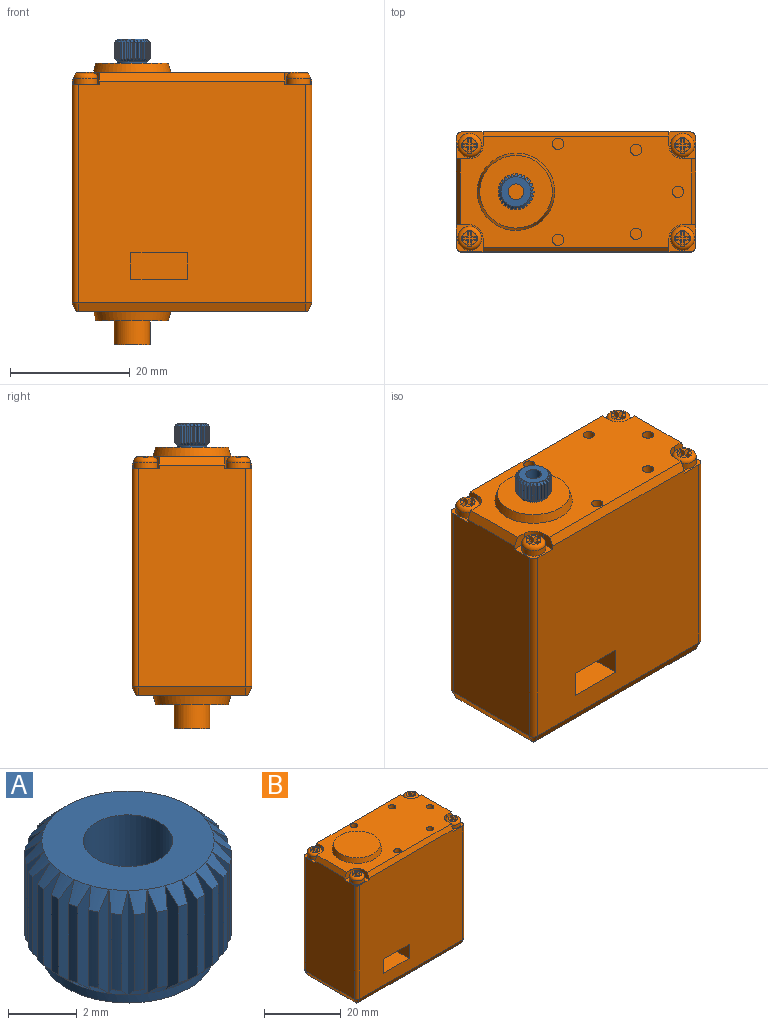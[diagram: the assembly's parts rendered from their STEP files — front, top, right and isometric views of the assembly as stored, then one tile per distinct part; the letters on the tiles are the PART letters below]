
ASSEMBLY  parts=2 mates=1
PART A: 144 faces, bbox 6x6x4 mm
  f0: cone r=3mm half-angle=45deg, axis (0,0,-1), area 0.3mm2, adj f1,f5,f7,f8
  f1: cylinder r=3mm len=2.7mm, axis (0,0,1), area 0.8mm2, adj f0,f2,f7,f8
  f2: cone r=2.5mm half-angle=45deg, axis (0,0,1), area 0.3mm2, adj f1,f6,f7,f8
  f3: plane 5x5mm, normal (0,0,-1), area 14.3mm2, adj f4,f6
  f4: cylinder r=1.3mm len=4mm, axis (0,0,1), area 32.7mm2, adj f3,f5
  f5: plane 5x5mm, normal (0,0,1), area 14.3mm2, adj f0,f4,f9,f14,f19,f24,f29,f34
  f6: cylinder r=2.5mm len=5mm, axis (0,0,1), area 4.7mm2, adj f2,f3,f11,f16,f21,f26,f31,f36
  f7: plane 3.72x0.53mm, normal (-0.23,0.97,0), area 1.7mm2, adj f0,f1,f2,f13
  f8: plane 3.72x0.53mm, normal (-0.23,-0.97,0), area 1.7mm2, adj f0,f1,f2,f142
  f9: cone r=3mm half-angle=45deg, axis (0,0,-1), area 0.3mm2, adj f5,f10,f12,f13
  f10: cylinder r=3mm len=2.7mm, axis (0,0,1), area 0.8mm2, adj f9,f11,f12,f13
  f11: cone r=2.5mm half-angle=45deg, axis (0,0,1), area 0.3mm2, adj f6,f10,f12,f13
  f12: plane 3.72x0.54mm, normal (-0.01,1,0), area 1.7mm2, adj f9,f10,f11,f18
  f13: plane 3.72x0.49mm, normal (-0.45,-0.9,0), area 1.7mm2, adj f7,f9,f10,f11
  f14: cone r=3mm half-angle=45deg, axis (0,0,-1), area 0.3mm2, adj f5,f15,f17,f18
  f15: cylinder r=3mm len=2.7mm, axis (0,0,1), area 0.8mm2, adj f14,f16,f17,f18
  f16: cone r=2.5mm half-angle=45deg, axis (0,0,1), area 0.3mm2, adj f6,f15,f17,f18
  f17: plane 3.72x0.53mm, normal (0.21,0.98,0), area 1.7mm2, adj f14,f15,f16,f23
  f18: plane 3.72x0.42mm, normal (-0.63,-0.77,0), area 1.7mm2, adj f12,f14,f15,f16
  f19: cone r=3mm half-angle=45deg, axis (0,0,-1), area 0.3mm2, adj f5,f20,f22,f23
  f20: cylinder r=3mm len=2.7mm, axis (0,0,1), area 0.8mm2, adj f19,f21,f22,f23
  f21: cone r=2.5mm half-angle=45deg, axis (0,0,1), area 0.3mm2, adj f6,f20,f22,f23
  f22: plane 3.72x0.49mm, normal (0.42,0.91,0), area 1.7mm2, adj f19,f20,f21,f28
  f23: plane 3.72x0.43mm, normal (-0.79,-0.61,0), area 1.7mm2, adj f17,f19,f20,f21
  f24: cone r=3mm half-angle=45deg, axis (0,0,-1), area 0.3mm2, adj f5,f25,f27,f28
  f25: cylinder r=3mm len=2.7mm, axis (0,0,1), area 0.8mm2, adj f24,f26,f27,f28
  f26: cone r=2.5mm half-angle=45deg, axis (0,0,1), area 0.3mm2, adj f6,f25,f27,f28
  f27: plane 3.72x0.43mm, normal (0.61,0.79,0), area 1.7mm2, adj f24,f25,f26,f33
  f28: plane 3.72x0.49mm, normal (-0.91,-0.42,0), area 1.7mm2, adj f22,f24,f25,f26
  f29: cone r=3mm half-angle=45deg, axis (0,0,-1), area 0.3mm2, adj f5,f30,f32,f33
  f30: cylinder r=3mm len=2.7mm, axis (0,0,1), area 0.8mm2, adj f29,f31,f32,f33
  f31: cone r=2.5mm half-angle=45deg, axis (0,0,1), area 0.3mm2, adj f6,f30,f32,f33
  f32: plane 3.72x0.42mm, normal (0.77,0.63,0), area 1.7mm2, adj f29,f30,f31,f38
  f33: plane 3.72x0.53mm, normal (-0.98,-0.21,0), area 1.7mm2, adj f27,f29,f30,f31
  f34: cone r=3mm half-angle=45deg, axis (0,0,-1), area 0.3mm2, adj f5,f35,f37,f38
  f35: cylinder r=3mm len=2.7mm, axis (0,0,1), area 0.8mm2, adj f34,f36,f37,f38
  f36: cone r=2.5mm half-angle=45deg, axis (0,0,1), area 0.3mm2, adj f6,f35,f37,f38
  f37: plane 3.72x0.49mm, normal (0.9,0.45,0), area 1.7mm2, adj f34,f35,f36,f43
  f38: plane 3.72x0.54mm, normal (-1,0.01,0), area 1.7mm2, adj f32,f34,f35,f36
  f39: cone r=3mm half-angle=45deg, axis (0,0,-1), area 0.3mm2, adj f5,f40,f42,f43
  f40: cylinder r=3mm len=2.7mm, axis (0,0,1), area 0.8mm2, adj f39,f41,f42,f43
  f41: cone r=2.5mm half-angle=45deg, axis (0,0,1), area 0.3mm2, adj f6,f40,f42,f43
  f42: plane 3.72x0.53mm, normal (0.97,0.23,0), area 1.7mm2, adj f39,f40,f41,f48
  f43: plane 3.72x0.53mm, normal (-0.97,0.23,0), area 1.7mm2, adj f37,f39,f40,f41
  f44: cone r=3mm half-angle=45deg, axis (0,0,-1), area 0.3mm2, adj f5,f45,f47,f48
  f45: cylinder r=3mm len=2.7mm, axis (0,0,1), area 0.8mm2, adj f44,f46,f47,f48
  f46: cone r=2.5mm half-angle=45deg, axis (0,0,1), area 0.3mm2, adj f6,f45,f47,f48
  f47: plane 3.72x0.54mm, normal (1,0.01,0), area 1.7mm2, adj f44,f45,f46,f53
  f48: plane 3.72x0.49mm, normal (-0.9,0.45,0), area 1.7mm2, adj f42,f44,f45,f46
  f49: cone r=3mm half-angle=45deg, axis (0,0,-1), area 0.3mm2, adj f5,f50,f52,f53
  f50: cylinder r=3mm len=2.7mm, axis (0,0,1), area 0.8mm2, adj f49,f51,f52,f53
  f51: cone r=2.5mm half-angle=45deg, axis (0,0,1), area 0.3mm2, adj f6,f50,f52,f53
  f52: plane 3.72x0.53mm, normal (0.98,-0.21,0), area 1.7mm2, adj f49,f50,f51,f58
  f53: plane 3.72x0.42mm, normal (-0.77,0.63,0), area 1.7mm2, adj f47,f49,f50,f51
  f54: cone r=3mm half-angle=45deg, axis (0,0,-1), area 0.3mm2, adj f5,f55,f57,f58
  f55: cylinder r=3mm len=2.7mm, axis (0,0,1), area 0.8mm2, adj f54,f56,f57,f58
  f56: cone r=2.5mm half-angle=45deg, axis (0,0,1), area 0.3mm2, adj f6,f55,f57,f58
  f57: plane 3.72x0.49mm, normal (0.91,-0.42,0), area 1.7mm2, adj f54,f55,f56,f63
  f58: plane 3.72x0.43mm, normal (-0.61,0.79,0), area 1.7mm2, adj f52,f54,f55,f56
  f59: cone r=3mm half-angle=45deg, axis (0,0,-1), area 0.3mm2, adj f5,f60,f62,f63
  f60: cylinder r=3mm len=2.7mm, axis (0,0,1), area 0.8mm2, adj f59,f61,f62,f63
  f61: cone r=2.5mm half-angle=45deg, axis (0,0,1), area 0.3mm2, adj f6,f60,f62,f63
  f62: plane 3.72x0.43mm, normal (0.79,-0.61,0), area 1.7mm2, adj f59,f60,f61,f68
  f63: plane 3.72x0.49mm, normal (-0.42,0.91,0), area 1.7mm2, adj f57,f59,f60,f61
  f64: cone r=3mm half-angle=45deg, axis (0,0,-1), area 0.3mm2, adj f5,f65,f67,f68
  f65: cylinder r=3mm len=2.7mm, axis (0,0,1), area 0.8mm2, adj f64,f66,f67,f68
  f66: cone r=2.5mm half-angle=45deg, axis (0,0,1), area 0.3mm2, adj f6,f65,f67,f68
  f67: plane 3.72x0.42mm, normal (0.63,-0.77,0), area 1.7mm2, adj f64,f65,f66,f73
  f68: plane 3.72x0.53mm, normal (-0.21,0.98,0), area 1.7mm2, adj f62,f64,f65,f66
  f69: cone r=3mm half-angle=45deg, axis (0,0,-1), area 0.3mm2, adj f5,f70,f72,f73
  f70: cylinder r=3mm len=2.7mm, axis (0,0,1), area 0.8mm2, adj f69,f71,f72,f73
  f71: cone r=2.5mm half-angle=45deg, axis (0,0,1), area 0.3mm2, adj f6,f70,f72,f73
  f72: plane 3.72x0.49mm, normal (0.45,-0.9,0), area 1.7mm2, adj f69,f70,f71,f78
  f73: plane 3.72x0.54mm, normal (0.01,1,0), area 1.7mm2, adj f67,f69,f70,f71
  f74: cone r=3mm half-angle=45deg, axis (0,0,-1), area 0.3mm2, adj f5,f75,f77,f78
  f75: cylinder r=3mm len=2.7mm, axis (0,0,1), area 0.8mm2, adj f74,f76,f77,f78
  f76: cone r=2.5mm half-angle=45deg, axis (0,0,1), area 0.3mm2, adj f6,f75,f77,f78
  f77: plane 3.72x0.53mm, normal (0.23,-0.97,0), area 1.7mm2, adj f74,f75,f76,f83
  f78: plane 3.72x0.53mm, normal (0.23,0.97,0), area 1.7mm2, adj f72,f74,f75,f76
  f79: cone r=3mm half-angle=45deg, axis (0,0,-1), area 0.3mm2, adj f5,f80,f82,f83
  f80: cylinder r=3mm len=2.7mm, axis (0,0,1), area 0.8mm2, adj f79,f81,f82,f83
  f81: cone r=2.5mm half-angle=45deg, axis (0,0,1), area 0.3mm2, adj f6,f80,f82,f83
  f82: plane 3.72x0.54mm, normal (0.01,-1,0), area 1.7mm2, adj f79,f80,f81,f88
  f83: plane 3.72x0.49mm, normal (0.45,0.9,0), area 1.7mm2, adj f77,f79,f80,f81
  f84: cone r=3mm half-angle=45deg, axis (0,0,-1), area 0.3mm2, adj f5,f85,f87,f88
  f85: cylinder r=3mm len=2.7mm, axis (0,0,1), area 0.8mm2, adj f84,f86,f87,f88
  f86: cone r=2.5mm half-angle=45deg, axis (0,0,1), area 0.3mm2, adj f6,f85,f87,f88
  f87: plane 3.72x0.53mm, normal (-0.21,-0.98,0), area 1.7mm2, adj f84,f85,f86,f93
  f88: plane 3.72x0.42mm, normal (0.63,0.77,0), area 1.7mm2, adj f82,f84,f85,f86
  f89: cone r=3mm half-angle=45deg, axis (0,0,-1), area 0.3mm2, adj f5,f90,f92,f93
  f90: cylinder r=3mm len=2.7mm, axis (0,0,1), area 0.8mm2, adj f89,f91,f92,f93
  f91: cone r=2.5mm half-angle=45deg, axis (0,0,1), area 0.3mm2, adj f6,f90,f92,f93
  f92: plane 3.72x0.49mm, normal (-0.42,-0.91,0), area 1.7mm2, adj f89,f90,f91,f98
  f93: plane 3.72x0.43mm, normal (0.79,0.61,0), area 1.7mm2, adj f87,f89,f90,f91
  f94: cone r=3mm half-angle=45deg, axis (0,0,-1), area 0.3mm2, adj f5,f95,f97,f98
  f95: cylinder r=3mm len=2.7mm, axis (0,0,1), area 0.8mm2, adj f94,f96,f97,f98
  f96: cone r=2.5mm half-angle=45deg, axis (0,0,1), area 0.3mm2, adj f6,f95,f97,f98
  f97: plane 3.72x0.43mm, normal (-0.61,-0.79,0), area 1.7mm2, adj f94,f95,f96,f103
  f98: plane 3.72x0.49mm, normal (0.91,0.42,0), area 1.7mm2, adj f92,f94,f95,f96
  f99: cone r=3mm half-angle=45deg, axis (0,0,-1), area 0.3mm2, adj f5,f100,f102,f103
  f100: cylinder r=3mm len=2.7mm, axis (0,0,1), area 0.8mm2, adj f99,f101,f102,f103
  f101: cone r=2.5mm half-angle=45deg, axis (0,0,1), area 0.3mm2, adj f6,f100,f102,f103
  f102: plane 3.72x0.42mm, normal (-0.77,-0.63,0), area 1.7mm2, adj f99,f100,f101,f108
  f103: plane 3.72x0.53mm, normal (0.98,0.21,0), area 1.7mm2, adj f97,f99,f100,f101
  f104: cone r=3mm half-angle=45deg, axis (0,0,-1), area 0.3mm2, adj f5,f105,f107,f108
  f105: cylinder r=3mm len=2.7mm, axis (0,0,1), area 0.8mm2, adj f104,f106,f107,f108
  f106: cone r=2.5mm half-angle=45deg, axis (0,0,1), area 0.3mm2, adj f6,f105,f107,f108
  f107: plane 3.72x0.49mm, normal (-0.9,-0.45,0), area 1.7mm2, adj f104,f105,f106,f113
  f108: plane 3.72x0.54mm, normal (1,-0.01,0), area 1.7mm2, adj f102,f104,f105,f106
  f109: cone r=3mm half-angle=45deg, axis (0,0,-1), area 0.3mm2, adj f5,f110,f112,f113
  f110: cylinder r=3mm len=2.7mm, axis (0,0,1), area 0.8mm2, adj f109,f111,f112,f113
  f111: cone r=2.5mm half-angle=45deg, axis (0,0,1), area 0.3mm2, adj f6,f110,f112,f113
  f112: plane 3.72x0.53mm, normal (-0.97,-0.23,0), area 1.7mm2, adj f109,f110,f111,f118
  f113: plane 3.72x0.53mm, normal (0.97,-0.23,0), area 1.7mm2, adj f107,f109,f110,f111
  f114: cone r=3mm half-angle=45deg, axis (0,0,-1), area 0.3mm2, adj f5,f115,f117,f118
  f115: cylinder r=3mm len=2.7mm, axis (0,0,1), area 0.8mm2, adj f114,f116,f117,f118
  f116: cone r=2.5mm half-angle=45deg, axis (0,0,1), area 0.3mm2, adj f6,f115,f117,f118
  f117: plane 3.72x0.54mm, normal (-1,-0.01,0), area 1.7mm2, adj f114,f115,f116,f123
  f118: plane 3.72x0.49mm, normal (0.9,-0.45,0), area 1.7mm2, adj f112,f114,f115,f116
  f119: cone r=3mm half-angle=45deg, axis (0,0,-1), area 0.3mm2, adj f5,f120,f122,f123
  f120: cylinder r=3mm len=2.7mm, axis (0,0,1), area 0.8mm2, adj f119,f121,f122,f123
  f121: cone r=2.5mm half-angle=45deg, axis (0,0,1), area 0.3mm2, adj f6,f120,f122,f123
  f122: plane 3.72x0.53mm, normal (-0.98,0.21,0), area 1.7mm2, adj f119,f120,f121,f128
  f123: plane 3.72x0.42mm, normal (0.77,-0.63,0), area 1.7mm2, adj f117,f119,f120,f121
  f124: cone r=3mm half-angle=45deg, axis (0,0,-1), area 0.3mm2, adj f5,f125,f127,f128
  f125: cylinder r=3mm len=2.7mm, axis (0,0,1), area 0.8mm2, adj f124,f126,f127,f128
  f126: cone r=2.5mm half-angle=45deg, axis (0,0,1), area 0.3mm2, adj f6,f125,f127,f128
  f127: plane 3.72x0.49mm, normal (-0.91,0.42,0), area 1.7mm2, adj f124,f125,f126,f133
  f128: plane 3.72x0.43mm, normal (0.61,-0.79,0), area 1.7mm2, adj f122,f124,f125,f126
  f129: cone r=3mm half-angle=45deg, axis (0,0,-1), area 0.3mm2, adj f5,f130,f132,f133
  f130: cylinder r=3mm len=2.7mm, axis (0,0,1), area 0.8mm2, adj f129,f131,f132,f133
  f131: cone r=2.5mm half-angle=45deg, axis (0,0,1), area 0.3mm2, adj f6,f130,f132,f133
  f132: plane 3.72x0.43mm, normal (-0.79,0.61,0), area 1.7mm2, adj f129,f130,f131,f138
  f133: plane 3.72x0.49mm, normal (0.42,-0.91,0), area 1.7mm2, adj f127,f129,f130,f131
  f134: cone r=3mm half-angle=45deg, axis (0,0,-1), area 0.3mm2, adj f5,f135,f137,f138
  f135: cylinder r=3mm len=2.7mm, axis (0,0,1), area 0.8mm2, adj f134,f136,f137,f138
  f136: cone r=2.5mm half-angle=45deg, axis (0,0,1), area 0.3mm2, adj f6,f135,f137,f138
  f137: plane 3.72x0.42mm, normal (-0.63,0.77,0), area 1.7mm2, adj f134,f135,f136,f143
  f138: plane 3.72x0.53mm, normal (0.21,-0.98,0), area 1.7mm2, adj f132,f134,f135,f136
  f139: cone r=3mm half-angle=45deg, axis (0,0,-1), area 0.3mm2, adj f5,f140,f142,f143
  f140: cylinder r=3mm len=2.7mm, axis (0,0,1), area 0.8mm2, adj f139,f141,f142,f143
  f141: cone r=2.5mm half-angle=45deg, axis (0,0,1), area 0.3mm2, adj f6,f140,f142,f143
  f142: plane 3.72x0.49mm, normal (-0.45,0.9,0), area 1.7mm2, adj f8,f139,f140,f141
  f143: plane 3.72x0.54mm, normal (-0.01,-1,0), area 1.7mm2, adj f137,f139,f140,f141
PART B: 154 faces, bbox 40x20x47 mm
  f0: plane 38x37mm, normal (0,-1,0), area 1359.1mm2, adj f14,f17,f26,f29,f108,f109,f113,f120
  f1: plane 38x37mm, normal (0,1,0), area 1359mm2, adj f18,f21,f22,f25,f106,f107,f114,f118
  f2: plane 38.6x18.6mm, normal (0,0,1), area 519.7mm2, adj f6,f14,f15,f16,f18,f19,f20,f22
  f3: plane 37x18mm, normal (1,0,0), area 661.8mm2, adj f15,f17,f19,f21,f106,f108,f117,f119
  f4: plane 37x18mm, normal (-1,0,0), area 661.8mm2, adj f23,f25,f27,f29,f107,f109,f110,f121
  f5: plane 38.6x18.6mm, normal (0,0,-1), area 570.2mm2, adj f8,f110,f111,f112,f113,f114,f115,f116
  f6: cone r=6.45mm half-angle=15deg, axis (0,0,-1), area 61mm2, adj f2,f7
  f7: plane 12.1x12.1mm, normal (0,0,1), area 114.9mm2, adj f6
  f8: cone r=6.45mm half-angle=15deg, axis (0,0,1), area 61mm2, adj f5,f9
  f9: plane 12.1x12.1mm, normal (0,0,-1), area 86.6mm2, adj f8,f12
  f10: plane 6x6mm, normal (0,0,-1), area 23mm2, adj f11,f12
  f11: cylinder r=1.3mm len=4mm, axis (0,0,1), area 32.7mm2, adj f10,f13
  f12: cylinder r=3mm len=6mm, axis (0,0,1), area 75.4mm2, adj f9,f10
  f13: plane 2.6x2.6mm, normal (0,0,-1), area 5.3mm2, adj f11
  f14: plane 2.25x2.1mm, normal (1,0,0), area 4.2mm2, adj f0,f2,f16,f17,f120
  f15: plane 2.25x2.1mm, normal (0,-1,0), area 4.2mm2, adj f2,f3,f16,f17,f119
  f16: cylinder r=2.25mm len=2.25mm, axis (0,0,1), area 7.4mm2, adj f2,f14,f15,f17
  f17: plane 4.5x4.5mm, normal (0,0,1), area 6.4mm2, adj f0,f3,f14,f15,f16,f92,f108
  f18: plane 2.25x2.1mm, normal (1,0,0), area 4.2mm2, adj f1,f2,f20,f21,f118
  f19: plane 2.25x2.1mm, normal (0,1,0), area 4.2mm2, adj f2,f3,f20,f21,f119
  f20: cylinder r=2.25mm len=2.25mm, axis (0,0,1), area 7.4mm2, adj f2,f18,f19,f21
  f21: plane 4.5x4.5mm, normal (0,0,1), area 6.4mm2, adj f1,f3,f18,f19,f20,f73,f106
  f22: plane 2.25x2.1mm, normal (-1,0,0), area 4.2mm2, adj f1,f2,f24,f25,f118
  f23: plane 2.25x2.1mm, normal (0,1,0), area 4.2mm2, adj f2,f4,f24,f25,f121
  f24: cylinder r=2.25mm len=2.25mm, axis (0,0,1), area 7.4mm2, adj f2,f22,f23,f25
  f25: plane 4.5x4.5mm, normal (0,0,1), area 6.4mm2, adj f1,f4,f22,f23,f24,f35,f107
  f26: plane 2.25x2.1mm, normal (-1,0,0), area 4.2mm2, adj f0,f2,f28,f29,f120
  f27: plane 2.25x2.1mm, normal (0,-1,0), area 4.2mm2, adj f2,f4,f28,f29,f121
  f28: cylinder r=2.25mm len=2.25mm, axis (0,0,1), area 7.4mm2, adj f2,f26,f27,f29
  f29: plane 4.5x4.5mm, normal (0,0,1), area 6.4mm2, adj f0,f4,f26,f27,f28,f54,f109
  f30: plane 0.78x0.78mm, normal (0,0,1), area 0.4mm2, adj f33,f41,f44
  f31: plane 0.78x0.78mm, normal (0,0,1), area 0.4mm2, adj f33,f37,f45
  f32: plane 0.78x0.78mm, normal (0,0,1), area 0.4mm2, adj f33,f36,f46
  f33: torus R=1.2mm, axis (0,0,1), area 13.1mm2, adj f30,f31,f32,f34,f35,f36,f37,f39
  f34: plane 0.78x0.78mm, normal (0,0,1), area 0.4mm2, adj f33,f39,f47
  f35: cylinder r=2mm len=4mm, axis (0,0,1), area 13.8mm2, adj f25,f33
  f36: plane 1.12x1mm, normal (-0.99,0,0.16), area 1mm2, adj f32,f33,f38,f40,f46
  f37: plane 1.12x1mm, normal (0.99,0,0.16), area 1mm2, adj f31,f33,f38,f40,f45
  f38: plane 2.3x2.3mm, normal (0,0,1), area 1.7mm2, adj f36,f37,f39,f40,f41,f42,f43,f44
  f39: plane 1.12x1mm, normal (-0.99,0,0.16), area 1mm2, adj f33,f34,f38,f42,f47
  f40: plane 0.99x0.73mm, normal (0,0.99,0.16), area 0.6mm2, adj f33,f36,f37,f38
  f41: plane 1.12x1mm, normal (0.99,0,0.16), area 1mm2, adj f30,f33,f38,f42,f44
  f42: plane 0.99x0.73mm, normal (0,-0.99,0.16), area 0.6mm2, adj f33,f38,f39,f41
  f43: plane 0.99x0.73mm, normal (0.99,0,0.16), area 0.6mm2, adj f33,f38,f44,f45
  f44: plane 1.12x1mm, normal (0,-0.99,0.16), area 1mm2, adj f30,f33,f38,f41,f43
  f45: plane 1.12x1mm, normal (0,0.99,0.16), area 1mm2, adj f31,f33,f37,f38,f43
  f46: plane 1.12x1mm, normal (0,0.99,0.16), area 1mm2, adj f32,f33,f36,f38,f48
  f47: plane 1.12x1mm, normal (0,-0.99,0.16), area 1mm2, adj f33,f34,f38,f39,f48
  f48: plane 0.99x0.73mm, normal (-0.99,0,0.16), area 0.6mm2, adj f33,f38,f46,f47
  f49: plane 0.78x0.78mm, normal (0,0,1), area 0.4mm2, adj f52,f60,f63
  f50: plane 0.78x0.78mm, normal (0,0,1), area 0.4mm2, adj f52,f56,f64
  f51: plane 0.78x0.78mm, normal (0,0,1), area 0.4mm2, adj f52,f55,f65
  f52: torus R=1.2mm, axis (0,0,1), area 13.1mm2, adj f49,f50,f51,f53,f54,f55,f56,f58
  f53: plane 0.78x0.78mm, normal (0,0,1), area 0.4mm2, adj f52,f58,f66
  f54: cylinder r=2mm len=4mm, axis (0,0,1), area 13.8mm2, adj f29,f52
  f55: plane 1.12x1mm, normal (-0.99,0,0.16), area 1mm2, adj f51,f52,f57,f59,f65
  f56: plane 1.12x1mm, normal (0.99,0,0.16), area 1mm2, adj f50,f52,f57,f59,f64
  f57: plane 2.3x2.3mm, normal (0,0,1), area 1.7mm2, adj f55,f56,f58,f59,f60,f61,f62,f63
  f58: plane 1.12x1mm, normal (-0.99,0,0.16), area 1mm2, adj f52,f53,f57,f61,f66
  f59: plane 0.99x0.73mm, normal (0,-0.99,0.16), area 0.6mm2, adj f52,f55,f56,f57
  f60: plane 1.12x1mm, normal (0.99,0,0.16), area 1mm2, adj f49,f52,f57,f61,f63
  f61: plane 0.99x0.73mm, normal (0,0.99,0.16), area 0.6mm2, adj f52,f57,f58,f60
  f62: plane 0.99x0.73mm, normal (0.99,0,0.16), area 0.6mm2, adj f52,f57,f63,f64
  f63: plane 1.12x1mm, normal (0,0.99,0.16), area 1mm2, adj f49,f52,f57,f60,f62
  f64: plane 1.12x1mm, normal (0,-0.99,0.16), area 1mm2, adj f50,f52,f56,f57,f62
  f65: plane 1.12x1mm, normal (0,-0.99,0.16), area 1mm2, adj f51,f52,f55,f57,f67
  f66: plane 1.12x1mm, normal (0,0.99,0.16), area 1mm2, adj f52,f53,f57,f58,f67
  f67: plane 0.99x0.73mm, normal (-0.99,0,0.16), area 0.6mm2, adj f52,f57,f65,f66
  f68: plane 0.78x0.78mm, normal (0,0,1), area 0.4mm2, adj f71,f79,f82
  f69: plane 0.78x0.78mm, normal (0,0,1), area 0.4mm2, adj f71,f75,f83
  f70: plane 0.78x0.78mm, normal (0,0,1), area 0.4mm2, adj f71,f74,f84
  f71: torus R=1.2mm, axis (0,0,1), area 13.1mm2, adj f68,f69,f70,f72,f73,f74,f75,f77
  f72: plane 0.78x0.78mm, normal (0,0,1), area 0.4mm2, adj f71,f77,f85
  f73: cylinder r=2mm len=4mm, axis (0,0,1), area 13.8mm2, adj f21,f71
  f74: plane 1.12x1mm, normal (0.99,0,0.16), area 1mm2, adj f70,f71,f76,f78,f84
  f75: plane 1.12x1mm, normal (-0.99,0,0.16), area 1mm2, adj f69,f71,f76,f78,f83
  f76: plane 2.3x2.3mm, normal (0,0,1), area 1.7mm2, adj f74,f75,f77,f78,f79,f80,f81,f82
  f77: plane 1.12x1mm, normal (0.99,0,0.16), area 1mm2, adj f71,f72,f76,f80,f85
  f78: plane 0.99x0.73mm, normal (0,0.99,0.16), area 0.6mm2, adj f71,f74,f75,f76
  f79: plane 1.12x1mm, normal (-0.99,0,0.16), area 1mm2, adj f68,f71,f76,f80,f82
  f80: plane 0.99x0.73mm, normal (0,-0.99,0.16), area 0.6mm2, adj f71,f76,f77,f79
  f81: plane 0.99x0.73mm, normal (-0.99,0,0.16), area 0.6mm2, adj f71,f76,f82,f83
  f82: plane 1.12x1mm, normal (0,-0.99,0.16), area 1mm2, adj f68,f71,f76,f79,f81
  f83: plane 1.12x1mm, normal (0,0.99,0.16), area 1mm2, adj f69,f71,f75,f76,f81
  f84: plane 1.12x1mm, normal (0,0.99,0.16), area 1mm2, adj f70,f71,f74,f76,f86
  f85: plane 1.12x1mm, normal (0,-0.99,0.16), area 1mm2, adj f71,f72,f76,f77,f86
  f86: plane 0.99x0.73mm, normal (0.99,0,0.16), area 0.6mm2, adj f71,f76,f84,f85
  f87: plane 0.78x0.78mm, normal (0,0,1), area 0.4mm2, adj f90,f98,f101
  f88: plane 0.78x0.78mm, normal (0,0,1), area 0.4mm2, adj f90,f94,f102
  f89: plane 0.78x0.78mm, normal (0,0,1), area 0.4mm2, adj f90,f93,f103
  f90: torus R=1.2mm, axis (0,0,1), area 13.1mm2, adj f87,f88,f89,f91,f92,f93,f94,f96
  f91: plane 0.78x0.78mm, normal (0,0,1), area 0.4mm2, adj f90,f96,f104
  f92: cylinder r=2mm len=4mm, axis (0,0,1), area 13.8mm2, adj f17,f90
  f93: plane 1.12x1mm, normal (0.99,0,0.16), area 1mm2, adj f89,f90,f95,f97,f103
  f94: plane 1.12x1mm, normal (-0.99,0,0.16), area 1mm2, adj f88,f90,f95,f97,f102
  f95: plane 2.3x2.3mm, normal (0,0,1), area 1.7mm2, adj f93,f94,f96,f97,f98,f99,f100,f101
  f96: plane 1.12x1mm, normal (0.99,0,0.16), area 1mm2, adj f90,f91,f95,f99,f104
  f97: plane 0.99x0.73mm, normal (0,-0.99,0.16), area 0.6mm2, adj f90,f93,f94,f95
  f98: plane 1.12x1mm, normal (-0.99,0,0.16), area 1mm2, adj f87,f90,f95,f99,f101
  f99: plane 0.99x0.73mm, normal (0,0.99,0.16), area 0.6mm2, adj f90,f95,f96,f98
  f100: plane 0.99x0.73mm, normal (-0.99,0,0.16), area 0.6mm2, adj f90,f95,f101,f102
  f101: plane 1.12x1mm, normal (0,0.99,0.16), area 1mm2, adj f87,f90,f95,f98,f100
  f102: plane 1.12x1mm, normal (0,-0.99,0.16), area 1mm2, adj f88,f90,f94,f95,f100
  f103: plane 1.12x1mm, normal (0,-0.99,0.16), area 1mm2, adj f89,f90,f93,f95,f105
  f104: plane 1.12x1mm, normal (0,0.99,0.16), area 1mm2, adj f90,f91,f95,f96,f105
  f105: plane 0.99x0.73mm, normal (0.99,0,0.16), area 0.6mm2, adj f90,f95,f103,f104
  f106: cylinder r=1mm len=36.4mm, axis (0,0,1), area 57.2mm2, adj f1,f3,f21,f116
  f107: cylinder r=1mm len=36.4mm, axis (0,0,-1), area 57.2mm2, adj f1,f4,f25,f112
  f108: cylinder r=1mm len=36.4mm, axis (0,0,-1), area 57.2mm2, adj f0,f3,f17,f115
  f109: cylinder r=1mm len=36.4mm, axis (0,0,1), area 57.2mm2, adj f0,f4,f29,f111
  f110: plane 18x1.5mm, normal (-0.91,0,-0.42), area 29.8mm2, adj f4,f5,f111,f112
  f111: cone r=0.3mm half-angle=25deg, axis (0,0,1), area 1.7mm2, adj f5,f109,f110,f113
  f112: cone r=0.3mm half-angle=25deg, axis (0,0,1), area 1.7mm2, adj f5,f107,f110,f114
  f113: plane 38x1.5mm, normal (0,-0.91,-0.42), area 62.9mm2, adj f0,f5,f111,f115
  f114: plane 38x1.5mm, normal (0,0.91,-0.42), area 62.9mm2, adj f1,f5,f112,f116
  f115: cone r=0.3mm half-angle=25deg, axis (0,0,1), area 1.7mm2, adj f5,f108,f113,f117
  f116: cone r=0.3mm half-angle=25deg, axis (0,0,1), area 1.7mm2, adj f5,f106,f114,f117
  f117: plane 18x1.5mm, normal (0.91,0,-0.42), area 29.8mm2, adj f3,f5,f115,f116
  f118: plane 31x1.5mm, normal (0,0.91,0.42), area 51.3mm2, adj f1,f2,f18,f22
  f119: plane 11x1.5mm, normal (0.91,0,0.42), area 18.2mm2, adj f2,f3,f15,f19
  f120: plane 31x1.5mm, normal (0,-0.91,0.42), area 51.3mm2, adj f0,f2,f14,f26
  f121: plane 11x1.5mm, normal (-0.91,0,0.42), area 18.2mm2, adj f2,f4,f23,f27
  f122: cylinder r=0.95mm len=9mm, axis (0,0,1), area 53.7mm2, adj f2,f123
  f123: plane 1.9x1.9mm, normal (0,0,1), area 2.8mm2, adj f122
  f124: cylinder r=0.95mm len=9mm, axis (0,0,1), area 53.7mm2, adj f2,f125
  f125: plane 1.9x1.9mm, normal (0,0,1), area 2.8mm2, adj f124
  f126: cylinder r=0.95mm len=9mm, axis (0,0,1), area 53.7mm2, adj f2,f127
  f127: plane 1.9x1.9mm, normal (0,0,1), area 2.8mm2, adj f126
  f128: cylinder r=0.95mm len=9mm, axis (0,0,1), area 53.7mm2, adj f2,f129
  f129: plane 1.9x1.9mm, normal (0,0,1), area 2.8mm2, adj f128
  f130: cylinder r=0.95mm len=9mm, axis (0,0,1), area 53.7mm2, adj f2,f131
  f131: plane 1.9x1.9mm, normal (0,0,1), area 2.8mm2, adj f130
  f132: cylinder r=0.95mm len=9mm, axis (0,0,-1), area 53.7mm2, adj f5,f133
  f133: plane 1.9x1.9mm, normal (0,0,-1), area 2.8mm2, adj f132
  f134: cylinder r=0.95mm len=9mm, axis (0,0,-1), area 53.7mm2, adj f5,f135
  f135: plane 1.9x1.9mm, normal (0,0,-1), area 2.8mm2, adj f134
  f136: cylinder r=0.95mm len=9mm, axis (0,0,-1), area 53.7mm2, adj f5,f137
  f137: plane 1.9x1.9mm, normal (0,0,-1), area 2.8mm2, adj f136
  f138: cylinder r=0.95mm len=9mm, axis (0,0,-1), area 53.7mm2, adj f5,f139
  f139: plane 1.9x1.9mm, normal (0,0,-1), area 2.8mm2, adj f138
  f140: cylinder r=0.95mm len=9mm, axis (0,0,-1), area 53.7mm2, adj f5,f141
  f141: plane 1.9x1.9mm, normal (0,0,-1), area 2.8mm2, adj f140
  f142: cylinder r=0.95mm len=9mm, axis (0,0,-1), area 53.7mm2, adj f5,f143
  f143: plane 1.9x1.9mm, normal (0,0,-1), area 2.8mm2, adj f142
  f144: plane 9.5x8mm, normal (0,0,-1), area 76mm2, adj f1,f145,f147,f148
  f145: plane 8x4.5mm, normal (1,0,0), area 36mm2, adj f1,f144,f146,f148
  f146: plane 9.5x8mm, normal (0,0,1), area 76mm2, adj f1,f145,f147,f148
  f147: plane 8x4.5mm, normal (-1,0,0), area 36mm2, adj f1,f144,f146,f148
  f148: plane 9.5x4.5mm, normal (0,1,0), area 42.8mm2, adj f144,f145,f146,f147
  f149: plane 9.5x8mm, normal (0,0,-1), area 76mm2, adj f0,f150,f152,f153
  f150: plane 8x4.5mm, normal (1,0,0), area 36mm2, adj f0,f149,f151,f153
  f151: plane 9.5x8mm, normal (0,0,1), area 76mm2, adj f0,f150,f152,f153
  f152: plane 8x4.5mm, normal (-1,0,0), area 36mm2, adj f0,f149,f151,f153
  f153: plane 9.5x4.5mm, normal (0,-1,0), area 42.8mm2, adj f149,f150,f151,f152
PLACE A rot(axis=(0,0,-1),26.5deg) t=(-1.16,-4.49,0.06)mm
PLACE B t=(-0.11,-0.02,0.06)mm fixed
MATE revolute A.f0 <-> B.f6  axis (0,0,-1) through (-10.11,-0.02,21.56)mm
